# Revit family: Bernhardt_Design-Tables-Multipurpose-Intersection_divider
name_source: partatom
category: Furniture
units: mm (PartAtom-declared; Revit-internal decimal feet)

## family parameters
Always vertical = Yes
Cut with Voids When Loaded = No
OmniClass Number = 23.40.20.00
OmniClass Title = General Furniture and Specialties
Room Calculation Point = No
Shared = No
Work Plane-Based = No

## types (6) — shared parameters
Default Elevation = 0.000"
Manufacturer = Bernhardt Design
Model = Intersection
URL = http://www.bernhardtdesign.com

## per-type parameters (varying)
| type | Catalog | SKU | Screen Half Width | Screen Width |
| Intersection - USF - divider for 66" table | INS-USF | INS-USF | 28.500" | 57.000" |
| Intersection - USB - divider for 42" table | INS-USB | INS-USB | 16.500" | 33.000" |
| Intersection - USC - divider for 48" table | INS-USC | INS-USC | 19.500" | 39.000" |
| Intersection - USD - divider for 54" table | INS-USD | INS-USD | 22.500" | 45.000" |
| Intersection - USE - divider for 60" table | INS-USE | INS-USE | 25.500" | 51.000" |
| Intersection - USG - divider for 72" table | INS-USG | INS-USG | 31.500" | 63.000" |

## geometry (parser evidence)
native form markers: Sweep x3
no freeform markers — native parametric forms only
